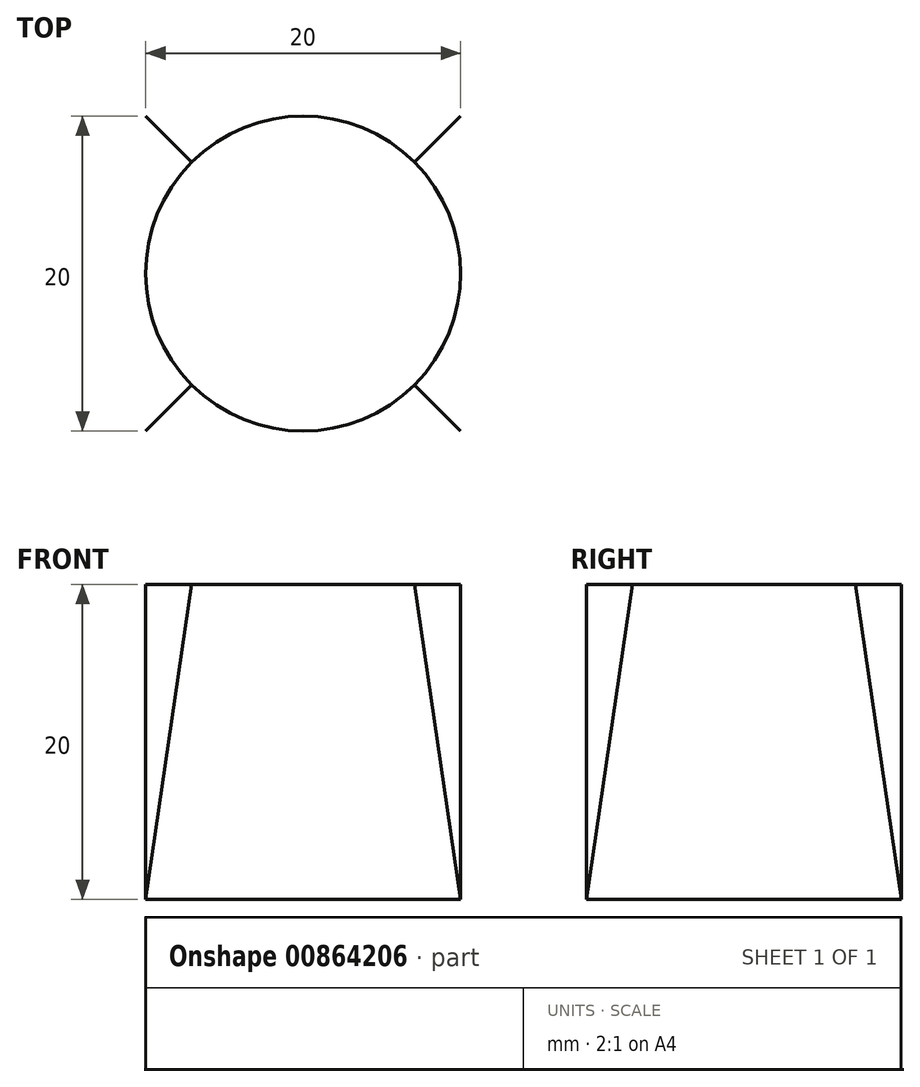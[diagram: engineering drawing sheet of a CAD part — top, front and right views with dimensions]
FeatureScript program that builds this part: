
annotation { "Feature Type Name" : "Feature", "Feature Type Description" : "" }
export const myFeature = defineFeature(function(context is Context, id is Id, definition is map)
    precondition{}
    {
        {
            var Q0;
            Q0=qCreatedBy(makeId("Top.planeOp"),FACE);
            var sketch = newSketch(context, id + "F0", { "sketchPlane" : qUnion([Q0])});
            skLineSegment(sketch, "E0.bottom", {"start": v(10, 10) * mm, "end": v(-10, 10) * mm});
            skLineSegment(sketch, "E0.top", {"start": v(10, -10) * mm, "end": v(-10, -10) * mm});
            skLineSegment(sketch, "E0.left", {"start": v(10, 10) * mm, "end": v(10, -10) * mm});
            skLineSegment(sketch, "E0.right", {"start": v(-10, 10) * mm, "end": v(-10, -10) * mm});
            skPoint(sketch, "E0.middle", {"position": v(0, 0) * mm});
            skSolve(sketch);
        }
        {
            var Q0;
            Q0=qCreatedBy(makeId("Top.planeOp"),FACE);
            cPlane(context, id + "F1", {"entities" : qUnion([Q0]), "cplaneType" : CPlaneType.OFFSET, "offset" : 20 * mm, "width" : 150 * mm, "height" : 150 * mm});
        }
        {
            var Q0;
            Q0=qCreatedBy(id+"F1.planeOp",FACE);
            var sketch = newSketch(context, id + "F2", { "sketchPlane" : qUnion([Q0])});
            skCircle(sketch, "E1", {"center": v(0, 0) * mm, "radius": 10 * mm});
            skSolve(sketch);
        }
        {
            var Q0;
            Q0=makeQuery(id+"F0.imprint","IMPRINT",FACE,{"disambiguationData":[TD([[makeQuery(id+"F0.imprint","IMPRINT",EDGE,{"derivedFrom":sQuery(id+"F0.wireOp",EDGE,"E0.bottom")}),1.0]])]});
            var Q1;
            Q1=makeQuery(id+"F2.imprint","IMPRINT",FACE,{"disambiguationData":[TD([[makeQuery(id+"F2.imprint","IMPRINT",EDGE,{"derivedFrom":sQuery(id+"F2.wireOp",EDGE,"E1")}),1.0]])]});
            loft(context, id + "F3", {"sheetProfilesArray" : [{ "sheetProfileEntities" : qUnion([Q0]) }, { "sheetProfileEntities" : qUnion([Q1]) }]});
        }
    });
